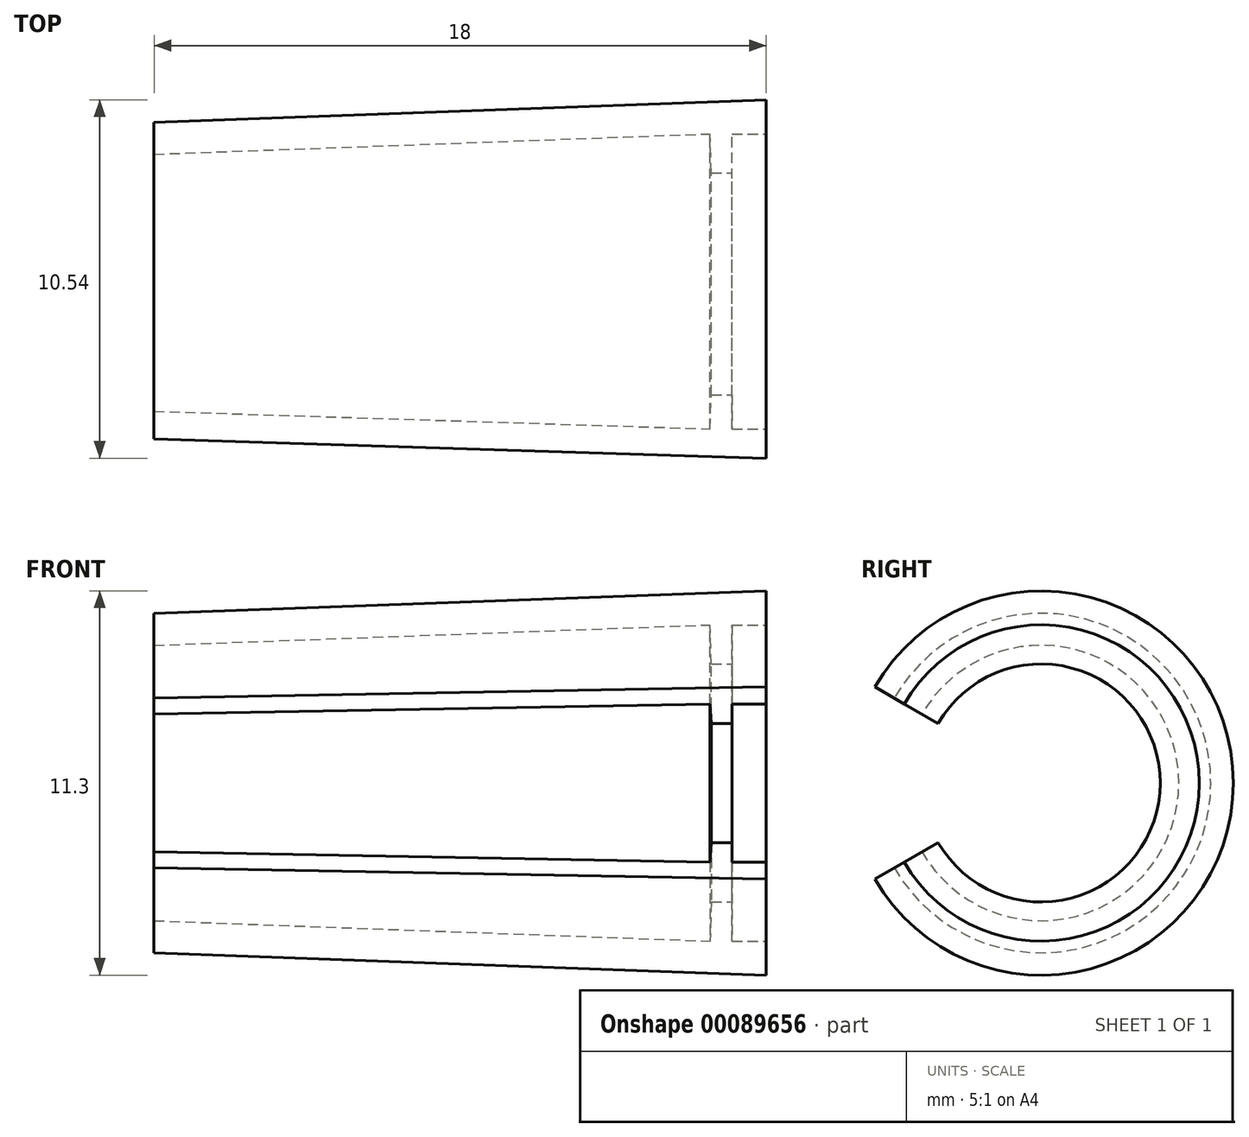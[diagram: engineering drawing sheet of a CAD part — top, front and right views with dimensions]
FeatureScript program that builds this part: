
annotation { "Feature Type Name" : "Feature", "Feature Type Description" : "" }
export const myFeature = defineFeature(function(context is Context, id is Id, definition is map)
    precondition{}
    {
        {
            var Q0;
            Q0=qCreatedBy(makeId("Top.planeOp"),FACE);
            var sketch = newSketch(context, id + "F0", { "sketchPlane" : qUnion([Q0])});
            skLineSegment(sketch, "E0", {"start": v(0, 0) * mm, "end": v(-23.38, 0) * mm, "construction": true});
            skLineSegment(sketch, "E1", {"start": v(-21.17, 4.05) * mm, "end": v(-4.82, 4.65) * mm});
            skLineSegment(sketch, "E2", {"start": v(-4.82, 4.65) * mm, "end": v(-4.78, 3.5) * mm});
            skLineSegment(sketch, "E3", {"start": v(-4.78, 3.5) * mm, "end": v(-4.17, 3.5) * mm});
            skLineSegment(sketch, "E4", {"start": v(-4.17, 3.5) * mm, "end": v(-4.17, 4.65) * mm});
            skLineSegment(sketch, "E5", {"start": v(-4.17, 4.65) * mm, "end": v(-3.17, 4.65) * mm});
            skLineSegment(sketch, "E6", {"start": v(-3.17, 4.65) * mm, "end": v(-3.17, 5.65) * mm});
            skLineSegment(sketch, "E7", {"start": v(-3.17, 5.65) * mm, "end": v(-21.17, 5) * mm});
            skLineSegment(sketch, "E8", {"start": v(-21.17, 5) * mm, "end": v(-21.17, 4.05) * mm});
            skSolve(sketch);
        }
        {
            var Q0;
            Q0=makeQuery(id+"F0.imprint","IMPRINT",FACE,{"disambiguationData":[TD([[makeQuery(id+"F0.imprint","IMPRINT",EDGE,{"derivedFrom":sQuery(id+"F0.wireOp",EDGE,"E1")}),1.0]])]});
            var Q1;
            Q1=sQuery(id+"F0.wireOp",EDGE,"E0");
            revolve(context, id + "F1", {"entities" : qUnion([Q0]), "axis" : qUnion([Q1]), "revolveType" : RevolveType.SYMMETRIC, "angle" : 300 * degree});
        }
    });
